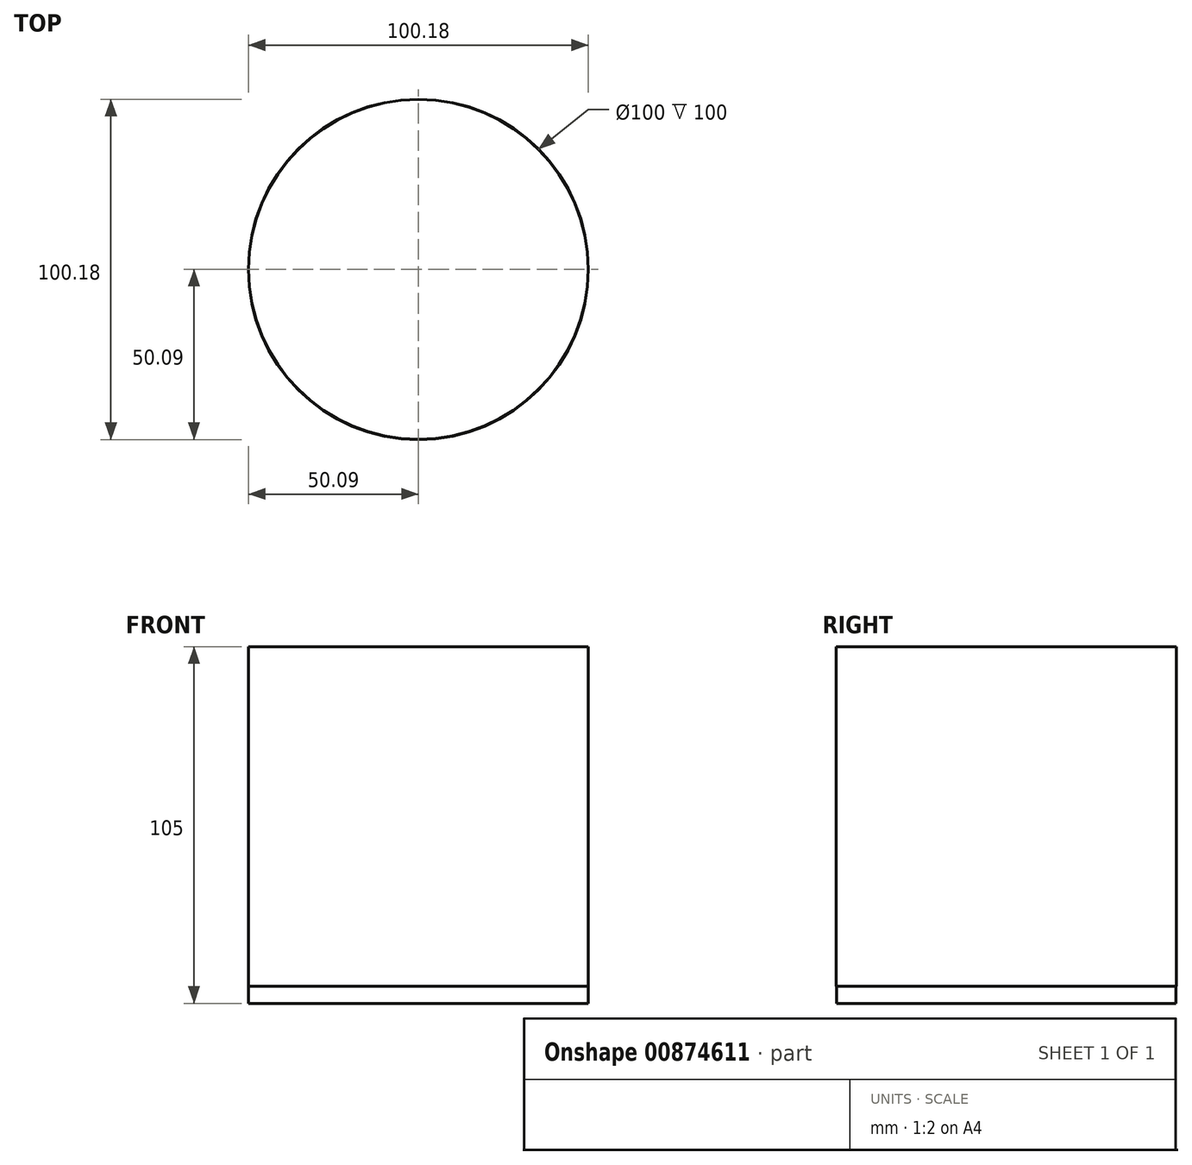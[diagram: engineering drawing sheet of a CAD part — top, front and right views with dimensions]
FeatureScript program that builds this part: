
annotation { "Feature Type Name" : "Feature", "Feature Type Description" : "" }
export const myFeature = defineFeature(function(context is Context, id is Id, definition is map)
    precondition{}
    {
        {
            var Q0;
            Q0=qCreatedBy(makeId("Top.planeOp"),FACE);
            var sketch = newSketch(context, id + "F0", { "sketchPlane" : qUnion([Q0])});
            skCircle(sketch, "E0", {"center": v(0, 0) * mm, "radius": 50 * mm});
            skSolve(sketch);
        }
        {
            var Q0;
            Q0 = qSketchRegion(id + "F0", true);
            extrude(context, id + "F1", {"entities" : qUnion([Q0]), "depth" : 5 * mm, "offsetDistance" : 25 * mm});
        }
        {
            var Q0;
            Q0=makeQuery(id+"F1.opExtrude","CAP_FACE",FACE,{"disambiguationData":[OSD([sQuery(id+"F0.wireOp",EDGE,"E0")])],"isStart":false});
            var sketch = newSketch(context, id + "F2", { "sketchPlane" : qUnion([Q0])});
            skCircle(sketch, "E1", {"center": v(0, 0) * mm, "radius": 50.1 * mm});
            skCircle(sketch, "E2", {"center": v(0, 0) * mm, "radius": 46.82 * mm});
            skSolve(sketch);
        }
        {
            var Q0;
            Q0=makeQuery(id+"F2.imprint","IMPRINT",FACE,{"disambiguationData":[TD([[makeQuery(id+"F2.imprint","IMPRINT",EDGE,{"derivedFrom":sQuery(id+"F2.wireOp",EDGE,"E1")}),1.0]])]});
            extrude(context, id + "F3", {"entities" : qUnion([Q0]), "depth" : 100 * mm, "offsetDistance" : 25 * mm});
        }
    });
